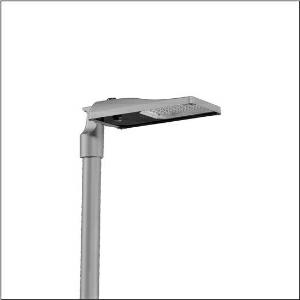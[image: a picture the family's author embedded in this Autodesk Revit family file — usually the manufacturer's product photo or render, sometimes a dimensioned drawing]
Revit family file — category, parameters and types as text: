
# Revit family: streetlight_sl_31_mini___st1_0a_5xh2d3at08ha_b443
name_source: partatom
category: Lighting Fixtures
units: mm (PartAtom-declared; Revit-internal decimal feet)

## family parameters
Cut with Voids When Loaded = No
Host = Face
Light Source = No
Part Type = Normal
Room Calculation Point = No
Round Connector Dimension = Use Diameter
Shared = No

## types (1)
- --- (1 x LED, 9230 lm, 68.3 W, 3000K)
    Apparent Load = 68 VA
    CIE Flux Codes = 37 72 97 100 100
    Color Rendering = 70
    Color Temperature = 3000K
    Default Elevation = 1800 mm
    Description = Streetlight SL 31 mini D4i mast luminaire for post-top, side-entry; light control with lens of PMMA; light distribution: ST1.0a, direct asymmetric distribution, for standard-compliant lighting for roads and squares; LED: luminous flux: 9.230lm, light colour: 730, colour temperature: 3000K; luminous efficacy: 135,1lm/W; control: pre-setting: logarithmic dimming characteristic, flexible luminous flux parameterisation, time-dependent luminous flux control, constant luminous flux control, power reduction, intelligent temperature release in ECG and LED module, overheat protection; luminaire housing, of diecast aluminium, Siteco® metallic grey (DB 702S), corrosivity category C5 high according to DIN EN ISO 12944; cover of toughened safety glass, transparent, mast flange of diecast aluminium, Siteco® metallic grey (DB 702S), spigot size: 76/60mm, mast flange included unmounted; with cable H07RN-F 2x 1.5mm², cable length: 8,5m, connection cable pre-assembled; mains connection: 220..240V, AC, 50/60Hz; power consumption (at start of service life): 68,3W / (at end of service life): 74,5W / (with reduced operation 50%): 29,5W; protection rating (complete): IP66; insulation class (complete): insulation class II (safety insulation); impact resistance: IK09; certification: CE, ENEC, ENEC+, VDE, UKCA, ZD4i; permissible operating ambient temperature for outdoor applications: -40..+50°C; packaging unit: 1 piece

Light Distribution: ST1.0a
    Height = 76 mm
    Lamp = 1 x LED
    Lamp Light Flux = 9230 lm
    Lamp Power = 68.3 W
    Lamp count = 1
    Length = 547 mm
    Luminous efficacy = 135 lm/W
    Manufacturer = Siteco
    ModVariant = No
    Model = 5XH2D3AT08HA
    Number of Poles = 1
    OnlyDefault = Yes
    Power Factor = 1
    Product Name = Streetlight SL 31 mini | ST1.0a
    Product group = mast luminaire | pylon top
    ProductGroupID = 6100
    Protection Class = Protection class II
    Protection Degree = IP 66
    RLX_Detail_Level = 1
    RLX_Emergency_Light_Flux = 0 lm
    RLX_Emergency_Type = 0
    RLX_Emergency_Type_DB = No
    RlxData = <blob elided: 39497 chars, md5=98040c1d>
    Socket = socket
    Standby Power = 0 W
    System Light Flux = 9230 lm
    System Power = 68 W
    Type Comments = factory setting: luminous flux: 100 % | dim-lin: 254 | 692 mA
    Type Image = l_1300332.jpg
    URL = http://relux.com
    VarID = @adj_019455
    Voltage = 0 V
    Weight = 0.00 kg
    Width = 265 mm

## geometry (parser evidence)
native form markers: Blend x4, Sweep x9
no freeform markers — native parametric forms only
